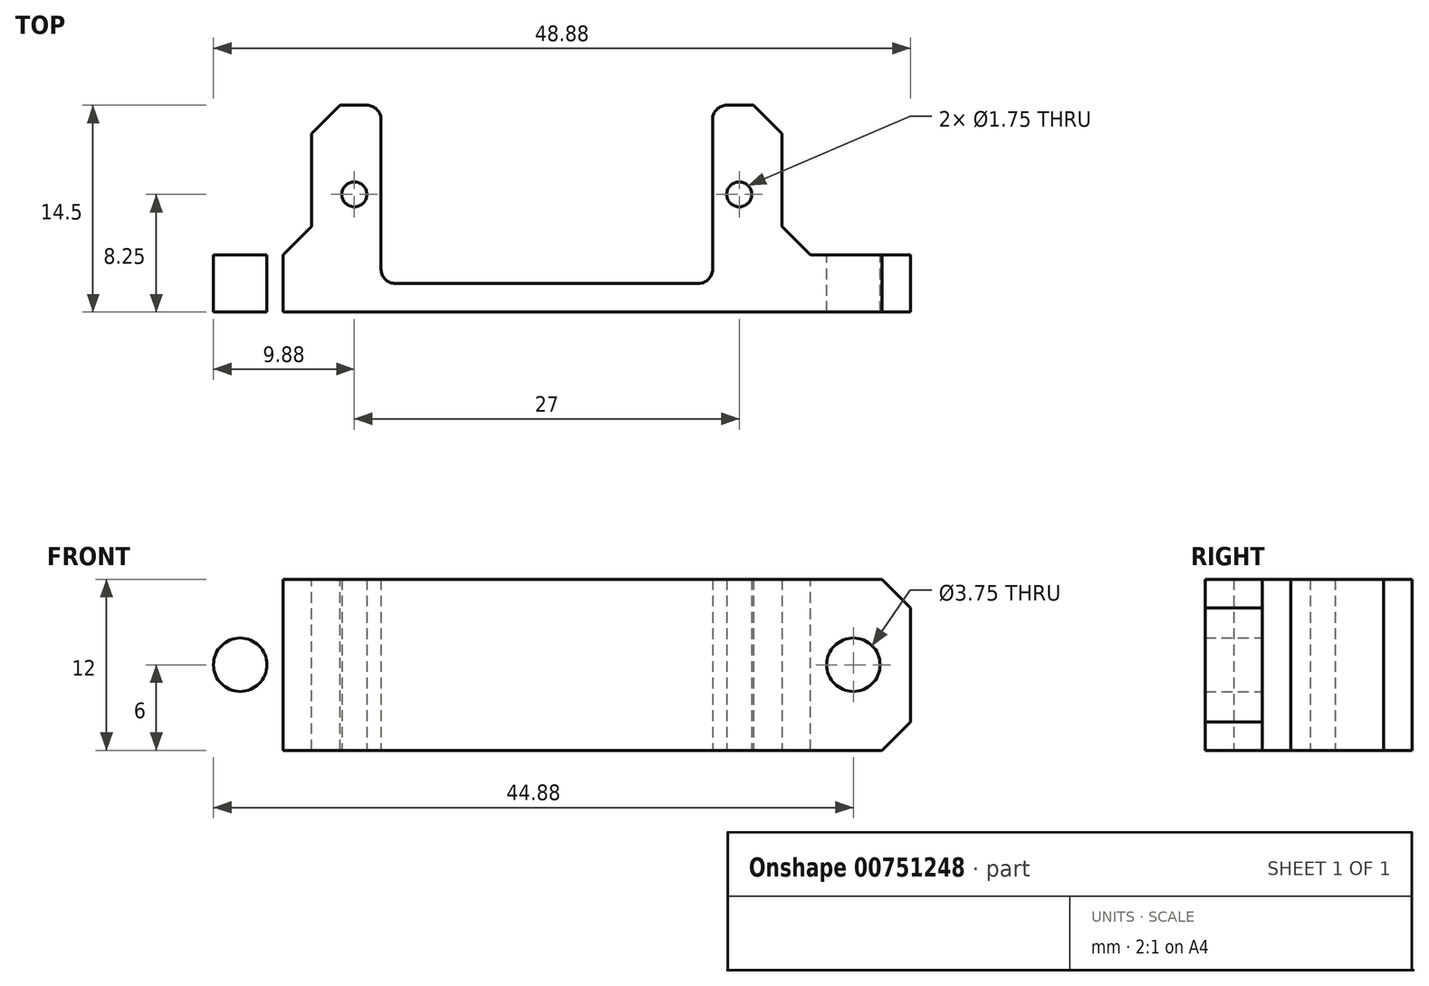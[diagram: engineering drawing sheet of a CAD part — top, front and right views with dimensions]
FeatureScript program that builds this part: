
annotation { "Feature Type Name" : "Feature", "Feature Type Description" : "" }
export const myFeature = defineFeature(function(context is Context, id is Id, definition is map)
    precondition{}
    {
        {
            var Q0;
            Q0=qCreatedBy(makeId("Top.planeOp"),FACE);
            var sketch = newSketch(context, id + "F0", { "sketchPlane" : qUnion([Q0])});
            skLineSegment(sketch, "E0.bottom", {"start": v(-16.5, 7.25) * mm, "end": v(16.5, 7.25) * mm});
            skLineSegment(sketch, "E0.top", {"start": v(-16.5, -7.25) * mm, "end": v(16.5, -7.25) * mm});
            skLineSegment(sketch, "E0.left", {"start": v(-16.5, 7.25) * mm, "end": v(-16.5, -7.25) * mm});
            skLineSegment(sketch, "E0.right", {"start": v(16.5, 7.25) * mm, "end": v(16.5, -7.25) * mm});
            skPoint(sketch, "E0.middle", {"position": v(0, 0) * mm});
            skLineSegment(sketch, "E1.bottom", {"start": v(-16.5, -3.25) * mm, "end": v(-25.5, -3.25) * mm});
            skLineSegment(sketch, "E1.top", {"start": v(-16.5, -7.25) * mm, "end": v(-25.5, -7.25) * mm});
            skLineSegment(sketch, "E1.left", {"start": v(-16.5, -3.25) * mm, "end": v(-16.5, -7.25) * mm});
            skLineSegment(sketch, "E1.right", {"start": v(-25.5, -3.25) * mm, "end": v(-25.5, -7.25) * mm});
            skLineSegment(sketch, "E2.MirrorCS", {"start": v(16.5, -3.25) * mm, "end": v(25.5, -3.25) * mm});
            skLineSegment(sketch, "E3.MirrorCS", {"start": v(16.5, -7.25) * mm, "end": v(25.5, -7.25) * mm});
            skLineSegment(sketch, "E4.MirrorCS", {"start": v(25.5, -3.25) * mm, "end": v(25.5, -7.25) * mm});
            skLineSegment(sketch, "E5.bottom", {"start": v(-11.62, 7.25) * mm, "end": v(11.62, 7.25) * mm});
            skLineSegment(sketch, "E5.top", {"start": v(-11.62, -5.25) * mm, "end": v(11.62, -5.25) * mm});
            skLineSegment(sketch, "E5.left", {"start": v(-11.62, 7.25) * mm, "end": v(-11.62, -5.25) * mm});
            skLineSegment(sketch, "E5.right", {"start": v(11.62, 7.25) * mm, "end": v(11.62, -5.25) * mm});
            skCircle(sketch, "E6", {"center": v(-13.5, 1) * mm, "radius": 0.88 * mm});
            skCircle(sketch, "E7.MirrorC", {"center": v(13.5, 1) * mm, "radius": 0.88 * mm});
            skLineSegment(sketch, "E8", {"start": v(-11.62, -5.25) * mm, "end": v(-16.5, -5.25) * mm});
            skLineSegment(sketch, "E9", {"start": v(11.62, -5.25) * mm, "end": v(16.5, -5.25) * mm});
            skSolve(sketch);
        }
        {
            var Q0;
            {var subQ1=sQuery(id+"F0.wireOp",EDGE,"E0.top");Q0=makeQuery(id+"F0.imprint","IMPRINT",FACE,{"disambiguationData":[TD([[makeQuery(id+"F0.imprint","IMPRINT",EDGE,{"derivedFrom":subQ1}),1.0]])]});}
            var Q1;
            Q1=makeQuery(id+"F0.imprint","IMPRINT",FACE,{"disambiguationData":[TD([[makeQuery(id+"F0.imprint","IMPRINT",EDGE,{"derivedFrom":sQuery(id+"F0.wireOp",EDGE,"E1.bottom")}),1.0]])]});
            var Q2;
            {var subQ2=sQuery(id+"F0.wireOp",EDGE,"E2.MirrorCS");Q2=makeQuery(id+"F0.imprint","IMPRINT",FACE,{"disambiguationData":[TD([[makeQuery(id+"F0.imprint","IMPRINT",EDGE,{"derivedFrom":subQ2}),-1.0]])]});}
            var Q3;
            {var subQ2=sQuery(id+"F0.wireOp",EDGE,"E0.left");Q3=makeQuery(id+"F0.imprint","IMPRINT",FACE,{"disambiguationData":[TD([[makeQuery(id+"F0.imprint","IMPRINT",EDGE,{"derivedFrom":subQ2}),1.0]])]});}
            var Q4;
            {var subQ0=sQuery(id+"F0.wireOp",EDGE,"E5.right");Q4=makeQuery(id+"F0.imprint","IMPRINT",FACE,{"disambiguationData":[TD([[makeQuery(id+"F0.imprint","IMPRINT",EDGE,{"derivedFrom":subQ0}),1.0]])]});}
            extrude(context, id + "F1", {"entities" : qUnion([Q0, Q1, Q2, Q3, Q4]), "flatOperationType" : FlatOperationType.REMOVE, "depth" : 12 * mm, "offsetDistance" : 25 * mm, "domain" : OperationDomain.MODEL});
        }
        {
            var Q0;
            Q0=makeQuery(id+"F1.opExtrude","SWEPT_EDGE",EDGE,{"disambiguationData":[OSD([sQuery(id+"F0.wireOp",EDGE,"E0.left"),sQuery(id+"F0.wireOp",EDGE,"E1.bottom"),sQuery(id+"F0.wireOp",EDGE,"E1.left")])]});
            var Q1;
            Q1=makeQuery(id+"F1.opExtrude","SWEPT_EDGE",EDGE,{"disambiguationData":[OSD([sQuery(id+"F0.wireOp",EDGE,"E0.right"),sQuery(id+"F0.wireOp",EDGE,"E2.MirrorCS")])]});
            var Q2;
            Q2=makeQuery(id+"F1.opExtrude","CAP_EDGE",EDGE,{"disambiguationData":[OSD([sQuery(id+"F0.wireOp",EDGE,"E4.MirrorCS")])],"isStart":false});
            var Q3;
            Q3=makeQuery(id+"F1.opExtrude","CAP_EDGE",EDGE,{"disambiguationData":[OSD([sQuery(id+"F0.wireOp",EDGE,"E4.MirrorCS")])],"isStart":true});
            var Q4;
            Q4=makeQuery(id+"F1.opExtrude","CAP_EDGE",EDGE,{"disambiguationData":[OSD([sQuery(id+"F0.wireOp",EDGE,"E1.right")])],"isStart":false});
            var Q5;
            Q5=makeQuery(id+"F1.opExtrude","CAP_EDGE",EDGE,{"disambiguationData":[OSD([sQuery(id+"F0.wireOp",EDGE,"E1.right")])],"isStart":true});
            var Q6;
            Q6=makeQuery(id+"F1.opExtrude","SWEPT_EDGE",EDGE,{"disambiguationData":[OSD([sQuery(id+"F0.wireOp",EDGE,"E0.bottom"),sQuery(id+"F0.wireOp",EDGE,"E0.right")])]});
            var Q7;
            Q7=makeQuery(id+"F1.opExtrude","SWEPT_EDGE",EDGE,{"disambiguationData":[OSD([sQuery(id+"F0.wireOp",EDGE,"E0.bottom"),sQuery(id+"F0.wireOp",EDGE,"E0.left")])]});
            chamfer(context, id + "F2", {"entities" : qUnion([Q0, Q1, Q2, Q3, Q4, Q5, Q6, Q7]), "width" : 2 * mm, "tangentPropagation" : true});
        }
        {
            var Q0;
            Q0=makeQuery(id+"F1.opExtrude","SWEPT_FACE",FACE,{"disambiguationData":[OSD([sQuery(id+"F0.wireOp",EDGE,"E1.bottom")])]});
            var sketch = newSketch(context, id + "F3", { "sketchPlane" : qUnion([Q0])});
            skCircle(sketch, "E10", {"center": v(-21.5, 6) * mm, "radius": 1.88 * mm});
            skLineSegment(sketch, "E11", {"start": v(-21.5, 6) * mm, "end": v(-25.5, 6) * mm, "construction": true});
            skLineSegment(sketch, "E12", {"start": v(-21.5, 6) * mm, "end": v(-17.5, 6) * mm, "construction": true});
            skCircle(sketch, "E13.MirrorC", {"center": v(21.5, 6) * mm, "radius": 1.88 * mm});
            skSolve(sketch);
        }
        {
            var Q0;
            Q0=makeQuery(id+"F3.imprint","IMPRINT",FACE,{"disambiguationData":[TD([[makeQuery(id+"F3.imprint","IMPRINT",EDGE,{"derivedFrom":sQuery(id+"F3.wireOp",EDGE,"E13.MirrorC")}),-1.0]])]});
            var Q1;
            Q1=makeQuery(id+"F3.imprint","IMPRINT",FACE,{"disambiguationData":[TD([[makeQuery(id+"F3.imprint","IMPRINT",EDGE,{"derivedFrom":sQuery(id+"F3.wireOp",EDGE,"E10")}),1.0]])]});
            var Q2;
            Q2=makeQuery(id+"F1.opExtrude","SWEPT_FACE",FACE,{"disambiguationData":[OSD([sQuery(id+"F0.wireOp",EDGE,"E0.top"),sQuery(id+"F0.wireOp",EDGE,"E1.top"),sQuery(id+"F0.wireOp",EDGE,"E3.MirrorCS")])]});
            extrude(context, id + "F4", {"entities" : qUnion([Q0, Q1]), "operationType" : NewBodyOperationType.REMOVE, "endBound" : BoundingType.UP_TO_SURFACE, "oppositeDirection" : true, "depth" : 25 * mm, "endBoundEntityFace" : qUnion([Q2]), "offsetDistance" : 25 * mm});
        }
        {
            var Q0;
            Q0=makeQuery(id+"F1.opExtrude","SWEPT_EDGE",EDGE,{"disambiguationData":[OSD([sQuery(id+"F0.wireOp",EDGE,"E5.top"),sQuery(id+"F0.wireOp",EDGE,"E5.right"),sQuery(id+"F0.wireOp",EDGE,"v9HbxVqt-2rQI-dspp-z2ZP-ibPVCHQ933eP")])]});
            var Q1;
            Q1=makeQuery(id+"F1.opExtrude","SWEPT_EDGE",EDGE,{"disambiguationData":[OSD([sQuery(id+"F0.wireOp",EDGE,"E5.top"),sQuery(id+"F0.wireOp",EDGE,"E5.left"),sQuery(id+"F0.wireOp",EDGE,"DVMDMKjG-olPc-v8IH-mmjh-vYbIOe0UTvFG")])]});
            var Q2;
            Q2=makeQuery(id+"F1.opExtrude","SWEPT_EDGE",EDGE,{"disambiguationData":[OSD([sQuery(id+"F0.wireOp",EDGE,"E0.bottom"),sQuery(id+"F0.wireOp",EDGE,"E5.bottom"),sQuery(id+"F0.wireOp",EDGE,"E5.left")])]});
            var Q3;
            Q3=makeQuery(id+"F1.opExtrude","SWEPT_EDGE",EDGE,{"disambiguationData":[OSD([sQuery(id+"F0.wireOp",EDGE,"E0.bottom"),sQuery(id+"F0.wireOp",EDGE,"E5.bottom"),sQuery(id+"F0.wireOp",EDGE,"E5.right")])]});
            var Q4;
            Q4=makeQuery(id+"Fj2hP9LWgfrMyZt_1.opExtrude","SWEPT_EDGE",EDGE,{"disambiguationData":[OSD([sQuery(id+"F0.wireOp",EDGE,"E0.bottom"),sQuery(id+"F0.wireOp",EDGE,"E5.bottom"),sQuery(id+"F0.wireOp",EDGE,"E5.left")])]});
            var Q5;
            Q5=makeQuery(id+"Fj2hP9LWgfrMyZt_1.opExtrude","SWEPT_EDGE",EDGE,{"disambiguationData":[OSD([sQuery(id+"F0.wireOp",EDGE,"E0.bottom"),sQuery(id+"F0.wireOp",EDGE,"E5.bottom"),sQuery(id+"F0.wireOp",EDGE,"E5.right")])]});
            var Q6;
            Q6=makeQuery(id+"Fj2hP9LWgfrMyZt_1.opExtrude","SWEPT_EDGE",EDGE,{"disambiguationData":[OSD([sQuery(id+"F0.wireOp",EDGE,"E5.top"),sQuery(id+"F0.wireOp",EDGE,"E5.left"),sQuery(id+"F0.wireOp",EDGE,"DVMDMKjG-olPc-v8IH-mmjh-vYbIOe0UTvFG")])]});
            var Q7;
            Q7=makeQuery(id+"Fj2hP9LWgfrMyZt_1.opExtrude","SWEPT_EDGE",EDGE,{"disambiguationData":[OSD([sQuery(id+"F0.wireOp",EDGE,"E5.top"),sQuery(id+"F0.wireOp",EDGE,"E5.right"),sQuery(id+"F0.wireOp",EDGE,"v9HbxVqt-2rQI-dspp-z2ZP-ibPVCHQ933eP")])]});
            fillet(context, id + "F5", {"entities" : qUnion([Q0, Q1, Q2, Q3, Q4, Q5, Q6, Q7]), "radius" : 1 * mm, "tangentPropagation" : true, "allowEdgeOverflow" : false});
        }
    });
